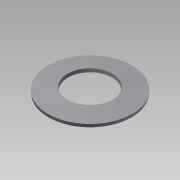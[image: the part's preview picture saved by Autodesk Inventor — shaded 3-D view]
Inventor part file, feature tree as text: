
AUTODESK INVENTOR PART (.ipt)
format: ipt  version: 2014 (Build 180170000, 170)  size: 96,768 bytes
history: native  units: mm
features: revolve x1, sketch x1
ambient origin geometry x8: Origin, YZ Plane, XZ Plane, XY Plane, X Axis, Y Axis, Z Axis, Center Point
bodies: Solid1 (feature_tree)
feature tree (2):
  revolve  "Revolution1"  [1 undecoded]
  sketch  "Sketch1"  dims[d2=0.3mm d3=0.55mm d4=4.0mm d5=2.1mm d6=90.0deg]
note: 1 required parameter value undecoded (feature->parameter linkage not recoverable at this tier; creation-order binding heuristic only, values carry confidence <= 0.55)
